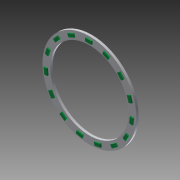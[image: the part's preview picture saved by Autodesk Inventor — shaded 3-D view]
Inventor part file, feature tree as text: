
AUTODESK INVENTOR PART (.ipt)
format: ipt  version: 2016 SP1 (Build 200210100, 210)  size: 151,552 bytes
history: native  units: mm
features: extrude x2, sketch x2, pattern_circular x1
ambient origin geometry x8: Origin, YZ Plane, XZ Plane, XY Plane, X Axis, Y Axis, Z Axis, Center Point
bodies: Solid1 (feature_tree)
feature tree (5):
  extrude  "Extrusion1"  Depth=50.0mm
  extrude  "Extrusion2"  Depth=2.0mm
  pattern_circular  "Circular Pattern1"  [2 undecoded]
  sketch  "Sketch1"  dims[d0=60.0mm d1=50.0mm]
  sketch  "Sketch2"  dims[d2=1.5mm d3=0.0mm d4=2.0mm d5=26.5mm d6=4.0mm d7=0.75mm d8=0.0mm d9=150.0mm d10=360.0deg]
note: 2 required parameter values undecoded (feature->parameter linkage not recoverable at this tier; creation-order binding heuristic only, values carry confidence <= 0.55)
